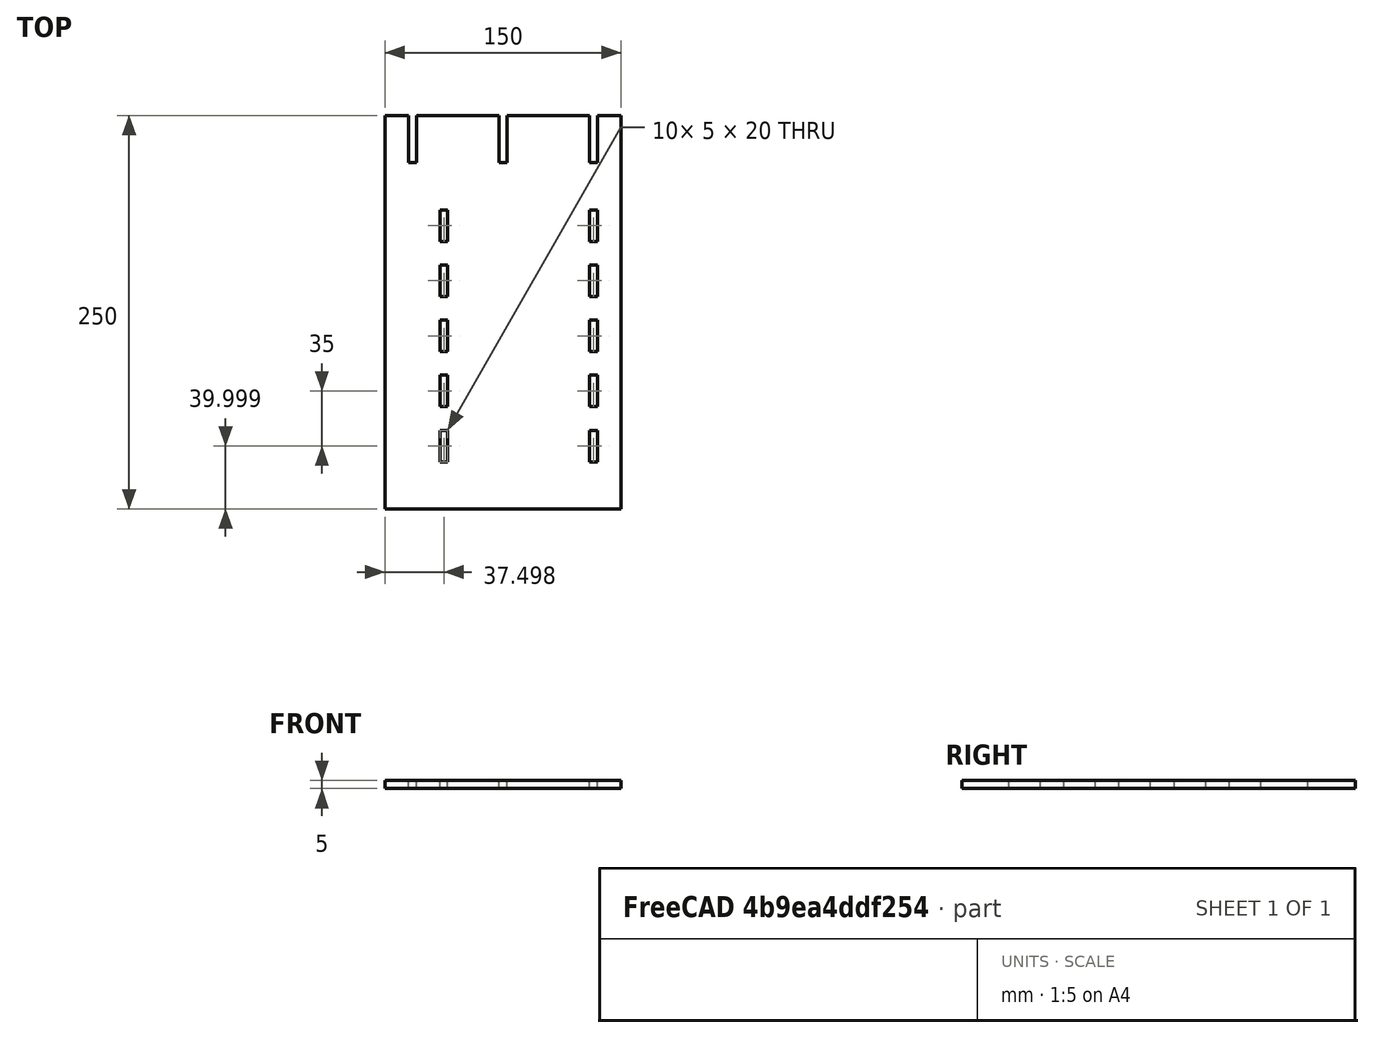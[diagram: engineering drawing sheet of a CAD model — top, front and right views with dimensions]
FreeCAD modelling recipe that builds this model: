
FCSTD DOCUMENT  (FreeCAD 0.17R13509 (Git))
Label: Support
License: All rights reserved
LicenseURL: http://en.wikipedia.org/wiki/All_rights_reserved
objects: Sketcher::SketchObject×1, PartDesign::Pad×1, PartDesign::Body×1
note: 4 computed .brp shape members not serialized (recipe doc carries the construction recipe); baked Part::Feature solids carry a one-line shape summary decoded from their .brp

FEATURE [Sketcher::SketchObject] Sketch
  MapMode = 5
  Support = -> [XY_Plane]
  sketch-geometry (70):
    g0: LineSegment [constr] StartX=-40.0817 StartY=73.4885 StartZ=0 EndX=-35.0817 EndY=73.4885 EndZ=0
    g1: LineSegment [constr] StartX=-35.0817 StartY=73.4885 StartZ=0 EndX=-35.0817 EndY=-106.512 EndZ=0
    g2: LineSegment [constr] StartX=-35.0817 StartY=-106.512 StartZ=0 EndX=-40.0817 EndY=-106.512 EndZ=0
    g3: LineSegment [constr] StartX=-40.0817 StartY=-106.512 StartZ=0 EndX=-40.0817 EndY=73.4885 EndZ=0
    g4: LineSegment [constr] StartX=54.9183 StartY=73.4885 StartZ=0 EndX=59.9183 EndY=73.4885 EndZ=0
    g5: LineSegment [constr] StartX=59.9183 StartY=73.4885 StartZ=0 EndX=59.9183 EndY=-106.512 EndZ=0
    g6: LineSegment [constr] StartX=59.9183 StartY=-106.512 StartZ=0 EndX=54.9183 EndY=-106.512 EndZ=0
    g7: LineSegment [constr] StartX=54.9183 StartY=-106.512 StartZ=0 EndX=54.9183 EndY=73.4885 EndZ=0
    g8: LineSegment StartX=74.9183 StartY=123.488 StartZ=0 EndX=74.9183 EndY=-126.512 EndZ=0
    g9: LineSegment StartX=74.9183 StartY=-126.512 StartZ=0 EndX=-75.0817 EndY=-126.512 EndZ=0
    g10: LineSegment StartX=-75.0817 StartY=-126.512 StartZ=0 EndX=-75.0817 EndY=123.488 EndZ=0
    g11: LineSegment StartX=-75.0817 StartY=123.488 StartZ=0 EndX=-60.0817 EndY=123.488 EndZ=0
    g12: LineSegment StartX=-60.0817 StartY=123.488 StartZ=0 EndX=-60.0817 EndY=93.4885 EndZ=0
    g13: LineSegment StartX=-60.0817 StartY=93.4885 StartZ=0 EndX=-55.0817 EndY=93.4885 EndZ=0
    g14: LineSegment StartX=-55.0817 StartY=93.4885 StartZ=0 EndX=-55.0817 EndY=123.488 EndZ=0
    g15: LineSegment StartX=-55.0817 StartY=123.488 StartZ=0 EndX=-2.58174 EndY=123.488 EndZ=0
    g16: LineSegment StartX=-2.58174 StartY=123.488 StartZ=0 EndX=-2.58174 EndY=93.4885 EndZ=0
    g17: LineSegment StartX=-2.58174 StartY=93.4885 StartZ=0 EndX=2.41826 EndY=93.4885 EndZ=0
    g18: LineSegment StartX=2.41826 StartY=93.4885 StartZ=0 EndX=2.41826 EndY=123.488 EndZ=0
    g19: LineSegment StartX=2.41826 StartY=123.488 StartZ=0 EndX=54.9183 EndY=123.488 EndZ=0
    g20: LineSegment StartX=54.9183 StartY=123.488 StartZ=0 EndX=54.9183 EndY=93.4885 EndZ=0
    g21: LineSegment StartX=54.9183 StartY=93.4885 StartZ=0 EndX=59.9183 EndY=93.4885 EndZ=0
    g22: LineSegment StartX=59.9183 StartY=93.4885 StartZ=0 EndX=59.9183 EndY=123.488 EndZ=0
    g23: LineSegment StartX=59.9183 StartY=123.488 StartZ=0 EndX=74.9183 EndY=123.488 EndZ=0
    g24: LineSegment [constr] StartX=-60.0817 StartY=123.488 StartZ=0 EndX=-55.0817 EndY=123.488 EndZ=0
    g25: LineSegment [constr] StartX=2.41826 StartY=123.488 StartZ=0 EndX=-2.58174 EndY=123.488 EndZ=0
    g26: LineSegment [constr] StartX=54.9183 StartY=123.488 StartZ=0 EndX=59.9183 EndY=123.488 EndZ=0
    g27: LineSegment [constr] StartX=-35.0817 StartY=73.4885 StartZ=0 EndX=54.9183 EndY=73.4885 EndZ=0
    g28: LineSegment [constr] StartX=-75.0817 StartY=-16.5115 StartZ=0 EndX=74.9183 EndY=-16.5115 EndZ=0
    g29: LineSegment StartX=-40.0817 StartY=-6.51154 StartZ=0 EndX=-35.0817 EndY=-6.51154 EndZ=0
    g30: LineSegment StartX=-35.0817 StartY=-6.51154 StartZ=0 EndX=-35.0817 EndY=-26.5115 EndZ=0
    g31: LineSegment StartX=-35.0817 StartY=-26.5115 StartZ=0 EndX=-40.0817 EndY=-26.5115 EndZ=0
    g32: LineSegment StartX=-40.0817 StartY=-26.5115 StartZ=0 EndX=-40.0817 EndY=-6.51154 EndZ=0
    g33: LineSegment StartX=-40.0817 StartY=28.4885 StartZ=0 EndX=-35.0817 EndY=28.4885 EndZ=0
    g34: LineSegment StartX=-35.0817 StartY=28.4885 StartZ=0 EndX=-35.0817 EndY=8.48846 EndZ=0
    g35: LineSegment StartX=-35.0817 StartY=8.48846 StartZ=0 EndX=-40.0817 EndY=8.48846 EndZ=0
    g36: LineSegment StartX=-40.0817 StartY=8.48846 StartZ=0 EndX=-40.0817 EndY=28.4885 EndZ=0
    g37: LineSegment StartX=-40.0817 StartY=63.4885 StartZ=0 EndX=-35.0817 EndY=63.4885 EndZ=0
    g38: LineSegment StartX=-35.0817 StartY=63.4885 StartZ=0 EndX=-35.0817 EndY=43.4885 EndZ=0
    g39: LineSegment StartX=-35.0817 StartY=43.4885 StartZ=0 EndX=-40.0817 EndY=43.4885 EndZ=0
    g40: LineSegment StartX=-40.0817 StartY=43.4885 StartZ=0 EndX=-40.0817 EndY=63.4885 EndZ=0
    g41: LineSegment StartX=-40.0817 StartY=-41.5115 StartZ=0 EndX=-35.0817 EndY=-41.5115 EndZ=0
    g42: LineSegment StartX=-35.0817 StartY=-41.5115 StartZ=0 EndX=-35.0817 EndY=-61.5115 EndZ=0
    g43: LineSegment StartX=-35.0817 StartY=-61.5115 StartZ=0 EndX=-40.0817 EndY=-61.5115 EndZ=0
    g44: LineSegment StartX=-40.0817 StartY=-61.5115 StartZ=0 EndX=-40.0817 EndY=-41.5115 EndZ=0
    g45: LineSegment StartX=-40.0817 StartY=-76.5115 StartZ=0 EndX=-35.0817 EndY=-76.5115 EndZ=0
    g46: LineSegment StartX=-35.0817 StartY=-76.5115 StartZ=0 EndX=-35.0817 EndY=-96.5115 EndZ=0
    g47: LineSegment StartX=-35.0817 StartY=-96.5115 StartZ=0 EndX=-40.0817 EndY=-96.5115 EndZ=0
    g48: LineSegment StartX=-40.0817 StartY=-96.5115 StartZ=0 EndX=-40.0817 EndY=-76.5115 EndZ=0
    g49: LineSegment StartX=54.9183 StartY=-6.51154 StartZ=0 EndX=59.9183 EndY=-6.51154 EndZ=0
    g50: LineSegment StartX=59.9183 StartY=-6.51154 StartZ=0 EndX=59.9183 EndY=-26.5115 EndZ=0
    g51: LineSegment StartX=59.9183 StartY=-26.5115 StartZ=0 EndX=54.9183 EndY=-26.5115 EndZ=0
    g52: LineSegment StartX=54.9183 StartY=-26.5115 StartZ=0 EndX=54.9183 EndY=-6.51154 EndZ=0
    g53: LineSegment StartX=54.9183 StartY=-41.5115 StartZ=0 EndX=59.9183 EndY=-41.5115 EndZ=0
    g54: LineSegment StartX=59.9183 StartY=-41.5115 StartZ=0 EndX=59.9183 EndY=-61.5115 EndZ=0
    g55: LineSegment StartX=59.9183 StartY=-61.5115 StartZ=0 EndX=54.9183 EndY=-61.5115 EndZ=0
    g56: LineSegment StartX=54.9183 StartY=-61.5115 StartZ=0 EndX=54.9183 EndY=-41.5115 EndZ=0
    g57: LineSegment StartX=54.9183 StartY=-76.5115 StartZ=0 EndX=59.9183 EndY=-76.5115 EndZ=0
    g58: LineSegment StartX=59.9183 StartY=-76.5115 StartZ=0 EndX=59.9183 EndY=-96.5115 EndZ=0
    g59: LineSegment StartX=59.9183 StartY=-96.5115 StartZ=0 EndX=54.9183 EndY=-96.5115 EndZ=0
    g60: LineSegment StartX=54.9183 StartY=-96.5115 StartZ=0 EndX=54.9183 EndY=-76.5115 EndZ=0
    g61: LineSegment StartX=54.9183 StartY=8.48846 StartZ=0 EndX=59.9183 EndY=8.48846 EndZ=0
    g62: LineSegment StartX=59.9183 StartY=8.48846 StartZ=0 EndX=59.9183 EndY=28.4885 EndZ=0
    g63: LineSegment StartX=59.9183 StartY=28.4885 StartZ=0 EndX=54.9183 EndY=28.4885 EndZ=0
    g64: LineSegment StartX=54.9183 StartY=28.4885 StartZ=0 EndX=54.9183 EndY=8.48846 EndZ=0
    g65: LineSegment StartX=54.9183 StartY=63.4885 StartZ=0 EndX=59.9183 EndY=63.4885 EndZ=0
    g66: LineSegment StartX=59.9183 StartY=63.4885 StartZ=0 EndX=59.9183 EndY=43.4885 EndZ=0
    g67: LineSegment StartX=59.9183 StartY=43.4885 StartZ=0 EndX=54.9183 EndY=43.4885 EndZ=0
    g68: LineSegment StartX=54.9183 StartY=43.4885 StartZ=0 EndX=54.9183 EndY=63.4885 EndZ=0
    g69: LineSegment [constr] StartX=-35.0817 StartY=63.4885 StartZ=0 EndX=54.9183 EndY=63.4885 EndZ=0
  constraints (205):
    c: Coincident(g0,g1)
    c: Coincident(g1,g2)
    c: Coincident(g2,g3)
    c: Coincident(g3,g0)
    c: Horizontal(g0)
    c: Horizontal(g2)
    c: Vertical(g1)
    c: Vertical(g3)
    c: Coincident(g4,g5)
    c: Coincident(g5,g6)
    c: Coincident(g6,g7)
    c: Coincident(g7,g4)
    c: Horizontal(g4)
    c: Horizontal(g6)
    c: Vertical(g5)
    c: Vertical(g7)
    c: Equal(g0,g4)
    c: DistanceX(g0,g0) = 5
    c: DistanceX(g0,g4) = 90
    c: Equal(g3,g7)
    c: DistanceY(g3,g3) = 180
    c: Coincident(g8,g9)
    c: Coincident(g9,g10)
    c: Horizontal(g9)
    c: Vertical(g8)
    c: Vertical(g10)
    c: DistanceX(g10,g8) = 150
    c: DistanceY(g10,g10) = 250
    c: DistanceX(g5,g8) = 15
    c: Coincident(g10,g11)
    c: Coincident(g11,g12)
    c: Vertical(g12)
    c: Coincident(g12,g13)
    c: Horizontal(g13)
    c: Coincident(g13,g14)
    c: Vertical(g14)
    c: Coincident(g14,g15)
    c: Horizontal(g15)
    c: Coincident(g15,g16)
    c: Vertical(g16)
    c: Coincident(g16,g17)
    c: Horizontal(g17)
    c: Coincident(g17,g18)
    c: Vertical(g18)
    c: Coincident(g18,g19)
    c: Horizontal(g19)
    c: Coincident(g19,g20)
    c: Vertical(g20)
    c: Coincident(g20,g21)
    c: Horizontal(g21)
    c: Coincident(g21,g22)
    c: Vertical(g22)
    c: Coincident(g22,g23)
    c: Coincident(g8,g23)
    c: Horizontal(g23)
    c: Horizontal(g11)
    c: Equal(g0,g13)
    c: Equal(g13,g17)
    c: Equal(g17,g21)
    c: Coincident(g24,g11)
    c: Coincident(g24,g14)
    c: Horizontal(g24)
    c: Coincident(g25,g18)
    c: Horizontal(g25)
    c: Coincident(g26,g19)
    c: Coincident(g26,g22)
    c: Horizontal(g26)
    c: Coincident(g25,g15)
    c: Equal(g20,g16)
    c: Equal(g16,g12)
    c: DistanceY(g12,g12) = 30
    c: DistanceX(g23,g23) = 15
    c: DistanceX(g11,g11) = 15
    c: DistanceY(g9,g2) = 20
    c: Coincident(g27,g0)
    c: Coincident(g27,g4)
    c: Horizontal(g27)
    c: Equal(g15,g19)
    c: DistanceX(g10) = -75.0817
    c: DistanceY(g10) = 123.488
    c: Symmetric(g0,g2,g28)
    c: Coincident(g29,g30)
    c: Coincident(g30,g31)
    c: Coincident(g31,g32)
    c: Coincident(g32,g29)
    c: Horizontal(g29)
    c: Horizontal(g31)
    c: Vertical(g30)
    c: Vertical(g32)
    c: PointOnObject(g29,g3)
    c: PointOnObject(g30,g1)
    c: Symmetric(g31,g29,g28)
    c: Coincident(g33,g34)
    c: Coincident(g34,g35)
    c: Coincident(g35,g36)
    c: Coincident(g36,g33)
    c: Horizontal(g33)
    c: Horizontal(g35)
    c: Vertical(g34)
    c: Vertical(g36)
    c: PointOnObject(g33,g3)
    c: PointOnObject(g34,g1)
    c: Coincident(g37,g38)
    c: Coincident(g38,g39)
    c: Coincident(g39,g40)
    c: Coincident(g40,g37)
    c: Horizontal(g37)
    c: Horizontal(g39)
    c: Vertical(g38)
    c: Vertical(g40)
    c: PointOnObject(g37,g3)
    c: PointOnObject(g38,g1)
    c: Coincident(g41,g42)
    c: Coincident(g42,g43)
    c: Coincident(g43,g44)
    c: Coincident(g44,g41)
    c: Horizontal(g41)
    c: Horizontal(g43)
    c: Vertical(g42)
    c: Vertical(g44)
    c: PointOnObject(g41,g3)
    c: PointOnObject(g42,g1)
    c: Coincident(g45,g46)
    c: Coincident(g46,g47)
    c: Coincident(g47,g48)
    c: Coincident(g48,g45)
    c: Horizontal(g45)
    c: Horizontal(g47)
    c: Vertical(g46)
    c: Vertical(g48)
    c: PointOnObject(g45,g3)
    c: PointOnObject(g46,g1)
    c: Equal(g48,g44)
    c: Equal(g44,g32)
    c: Equal(g32,g36)
    c: Equal(g36,g40)
    c: DistanceY(g30,g30) = 20
    c: DistanceY(g29,g34) = 15
    c: DistanceY(g33,g38) = 15
    c: DistanceY(g41,g30) = 15
    c: DistanceY(g45,g42) = 15
    c: Coincident(g49,g50)
    c: Coincident(g50,g51)
    c: Coincident(g51,g52)
    c: Coincident(g52,g49)
    c: Horizontal(g49)
    c: Horizontal(g51)
    c: Vertical(g50)
    c: Vertical(g52)
    c: PointOnObject(g49,g7)
    c: PointOnObject(g50,g5)
    c: Coincident(g53,g54)
    c: Coincident(g54,g55)
    c: Coincident(g55,g56)
    c: Coincident(g56,g53)
    c: Horizontal(g53)
    c: Horizontal(g55)
    c: Vertical(g54)
    c: Vertical(g56)
    c: PointOnObject(g53,g7)
    c: PointOnObject(g54,g5)
    c: Coincident(g57,g58)
    c: Coincident(g58,g59)
    c: Coincident(g59,g60)
    c: Coincident(g60,g57)
    c: Horizontal(g57)
    c: Horizontal(g59)
    c: Vertical(g58)
    c: Vertical(g60)
    c: PointOnObject(g57,g7)
    c: PointOnObject(g58,g5)
    c: Coincident(g61,g62)
    c: Coincident(g62,g63)
    c: Coincident(g63,g64)
    c: Coincident(g64,g61)
    c: Horizontal(g61)
    c: Horizontal(g63)
    c: Vertical(g62)
    c: Vertical(g64)
    c: PointOnObject(g61,g7)
    c: PointOnObject(g62,g5)
    c: Coincident(g65,g66)
    c: Coincident(g66,g67)
    c: Coincident(g67,g68)
    c: Coincident(g68,g65)
    c: Horizontal(g65)
    c: Horizontal(g67)
    c: Vertical(g66)
    c: Vertical(g68)
    c: PointOnObject(g65,g7)
    c: PointOnObject(g66,g5)
    c: Equal(g60,g56)
    c: Equal(g56,g52)
    c: Equal(g52,g64)
    c: Equal(g64,g68)
    c: DistanceY(g52,g52) = 20
    c: DistanceY(g49,g61) = 15
    c: DistanceY(g63,g67) = 15
    c: DistanceY(g53,g51) = 15
    c: DistanceY(g57,g55) = 15
    c: PointOnObject(g28,g8)
    c: PointOnObject(g28,g10)
    c: Coincident(g69,g37)
    c: Coincident(g69,g65)
    c: Horizontal(g69)
FEATURE [PartDesign::Pad] Pad
  Length = 5
  Length2 = 100
  Profile = -> Sketch
  Refine = true
  Type = 0
FEATURE [PartDesign::Body] Body
  Group = -> [Sketch,Pad]
  Origin = -> Origin
  Tip = -> Pad
